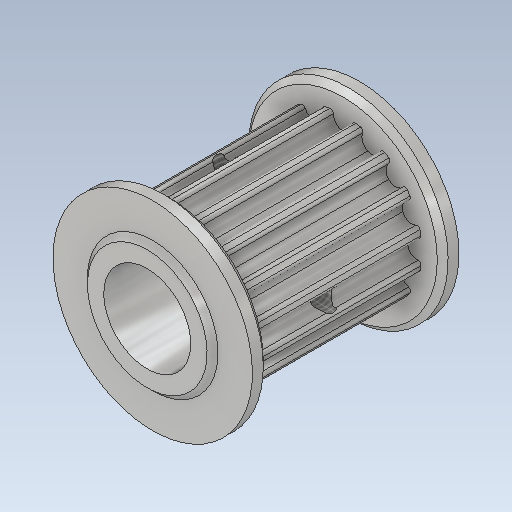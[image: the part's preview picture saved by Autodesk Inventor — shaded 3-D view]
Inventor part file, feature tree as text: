
AUTODESK INVENTOR PART (.ipt)
format: ipt  version: 2020.1 (Build 241239000, 239)  size: 466,944 bytes
history: native  units: mm
features: sketch x4, extrude x3, other x2, plane x2, pattern_circular x2, revolve x1, chamfer x1, mirror x1, thread x1
ambient origin geometry x8: Origin, YZ Plane, XZ Plane, XY Plane, X Axis, Y Axis, Z Axis, Center Point
bodies: Body1 (feature_tree)
feature tree (17):
  other  "gates_P16-3M-09AL.ipt"
  extrude  "Extrusion7"  Depth=10.0mm TaperAngle=0.0deg
  extrude  "Extrusion8"  Depth=15.0mm TaperAngle=0.0deg
  sketch  "Sketch15"  dims[d57=2.0mm d58=1.5mm]
  other  "Work Axis2"
  revolve  "Revolution2"  [1 undecoded]
  chamfer  "Chamfer2"  Distance=0.5mm
  plane  "Work Plane3"
  mirror  "Mirror1"
  plane  "Work Plane4"
  extrude  "Extrusion9"  TaperAngle=90.0deg  [1 undecoded]
  thread  "Thread2"  [1 undecoded]
  pattern_circular  "Circular Pattern1"  [2 undecoded]
  pattern_circular  "Circular Pattern2"  [2 undecoded]
  sketch  "Sketch1"  dims[d51=10.0mm d52=16.0mm d53=0.0mm]
  sketch  "Sketch14"  dims[d54=8.0mm d55=15.0mm d56=0.0mm]
  sketch  "Sketch16"  dims[d59=2.0mm d60=0.5mm d61=90.0deg d62=0.5mm d63=2.0mm d64=45.0deg d65=2.0mm d66=15.0mm d67=0.0mm d68=10.0mm d69=0.0mm d70=20.0mm d71=19.626227mm d73=20.0mm d74=135.0deg]
note: 7 required parameter values undecoded (feature->parameter linkage not recoverable at this tier; creation-order binding heuristic only, values carry confidence <= 0.55)